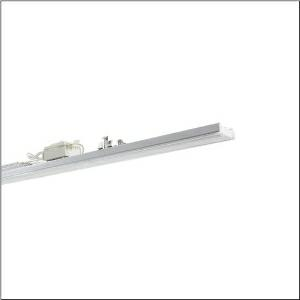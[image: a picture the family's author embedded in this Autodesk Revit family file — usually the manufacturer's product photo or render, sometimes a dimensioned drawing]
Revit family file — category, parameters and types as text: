
# Revit family: licross_11_recessed_mo_51tl12dn4axgd
name_source: partatom
category: Lighting Fixtures
units: mm (PartAtom-declared; Revit-internal decimal feet)

## family parameters
Cut with Voids When Loaded = No
Host = Face
Light Source = No
Part Type = Normal
Room Calculation Point = No
Round Connector Dimension = Use Diameter
Shared = No

## types (1)
- --- (1 x LED, 1540 lm, 9.2 W, 4000K)
    Apparent Load = 9 VA
    CIE Flux Codes = 67 92 99 100 100
    Color Rendering = 80
    Color Temperature = 4000K
    Default Elevation = 1800 mm
    Description = Licross 11 Recessed MO, luminaire insert, of sheet steel, coil coated, white, length: 1.500mm, width: 66mm, height: 67mm, LED rated luminous flux: 10.240lm, light colour: 840, SDCM (Standard Deviation of Colour Matching)MacAdam ≤ 2 SDCM (initial), control gear: DALI 2 (for two DALI lines), with plug, 6-pole, with phase selection, mains connection: 220..240V, AC/DC, 0/50..60Hz, rated input power: 57W, without changeover relay, for emergency light function, for central battery installations according to EN 60598-2-22, internal wiring halogen-free, primary optical cover: cover, of PMMA, light emission: direct distribution, primary light characteristic: symmetric, protection rating (complete): IP40, insulation class (complete): insulation class I (protective earthing), certification: CE, ENEC, VDE, UKCA, protection symbol: D if used in an environment without relevant dust loads with corresponding accessories, impact resistance: IK06, permissible ambient temperature for indoor applications: -25..+35°C, standard: EN 60598-2-22, corresponds to IFS (International Featured Standards) requirements for safety and quality in the food industry, reducing of maximum allowable ambient temperature of 5°C with ceiling mounting, LABS conformity tested according to VDMA 24364:2018-05, The light source and the operating device comply with the requirements of the Ecodesign Regulation (EU) 2019/2020 and are replaceable in accordance with this regulation, packaging unit: 1 piece
    Height = 58 mm
    Lamp = 1 x LED
    Lamp Light Flux = 1540 lm
    Lamp Power = 9.2 W
    Lamp count = 1
    Length = 1500 mm
    Luminous efficacy = 167 lm/W
    Manufacturer = Siteco
    ModVariant = No
    Model = 51TL12DN4AXGD
    Mounting Place = Ceiling
    Mounting Type = Pendant
    Number of Poles = 1
    OnlyDefault = Yes
    Power Factor = 1
    Product Name = Licross 11 Recessed MO
    Product group = luminaire insert | ceiling pendant
    ProductGroupID = 901
    Protection Class = Protection class I
    Protection Degree = IP 40
    RLX_Detail_Level = 1
    RLX_Emergency_Light_Flux = 0 lm
    RLX_Emergency_Type = 0
    RLX_Emergency_Type_DB = No
    RlxData = <blob elided: 25089 chars, md5=c245938a>
    Socket = socket
    Standby Power = 0 W
    System Light Flux = 1540 lm
    System Power = 9 W
    Type Comments = : DC mode (central or group accumulator) initial emergency light level
    Type Image = l_1296930.jpg
    URL = http://relux.com
    VarID = @adj_091447
    Voltage = 0 V
    Weight = 0.00 kg
    Width = 66 mm

## geometry (parser evidence)
native form markers: Blend x4, Sweep x12
no freeform markers — native parametric forms only
